# Revit family: IS_Melange_A4268_BIM_DE
name_source: partatom
category: Plumbing Fixtures
revit_build: Autodesk Revit MEP 2016 (Build: 20161004_0715(x64)
units: mm (PartAtom-declared; Revit-internal decimal feet)

## family parameters
Always vertical = No
Cut with Voids When Loaded = No
OmniClass Number = 23.45.55.17
OmniClass Title = Mixing Faucets
Part Type = Normal
Room Calculation Point = No
Round Connector Dimension = Use Diameter
Shared = No
Work Plane-Based = No

## types (1)
- A4268AA - IS Bidetarmatur MELANGE, m.Ablgarn., Ausld. 113mm, Chrom
    Accessories = www.idealstandard.de\ersatzteile
    Assembly Code = C1030200
    AssetType = Fest
    BIMobject category = Taps & Mixers
    BOSUseNativeGeometries = 1
    BarCode = 4015413316613
    Brand = Ideal Standard
    Brand url = http://www.idealstandard.de
    Color = Chrome
    Cost = 0 $
    CurrencyUnit = €
    CurrentRevision = 1
    Date of publishing = 15/09/2017
    Description = A4268AA MELANGE single lever bidet mixer
    DurationUnit = Jahr
    EAN code = https://4015413316613
    Edition number = 1
    ExpectedLife = 25
    Features = MELANGE single lever bidet mixer
    Finish = Chrome
    IFC Classification = Sanitary Terminal
    Installation instructions = http://www.idealstandard.de
    InstallationInstructions = www.idealstandard.de\produkte
    MainColor = Chrome
    Manufacturer = www.idealstandard.de\produkte
    Manufacturer name = Ideal Standard
    ManufacturerURL = http://www.idealstandard.de
    Material = Brass
    Material main = Brass
    Model = A4268AA
    ModelNumber = A4268AA
    ModelReference = A4268AA MELANGE single lever bidet mixer
    NettWeight = 2,35 kg
    Nominal height = 0
    Nominal width = 0
    NominalHeight = 128 mm
    NominalLength = 157 mm
    NominalWidth = 93 mm
    Product Guid = 30327c98-35da-4949-88fa-b4f7433397b3
    Product SKU = A4268
    Product data url = https://bimobject.com
    Product family = MELANGE
    Product group = Bidet Mixer
    Product name = MELANGE single lever bidet mixer
    Product url = http://www.idealstandard.de
    ProductInformation = www.idealstandard.de\produkte
    QR code = http://bimobject.com
    Shape = Sculptured
    Size = 128 X 157 X 93mm
    Space = Intern
    SpareParts = www.idealstandard.de/ersatzteile
    Technical description = http://www.idealstandard.de
    URL = http://www.idealstandard.de
    Uniclass2015Code = Pr_40_20_87_11
    Uniclass2015Title = Bidet taps
    Uniclass2015Version = Products v1.1
    Version = 1
    VolumeUnits = Litres
    Weight Net (Kg) = 2.35

## geometry (parser evidence)
native form markers: Blend x4, Sweep x1
no freeform markers — native parametric forms only
